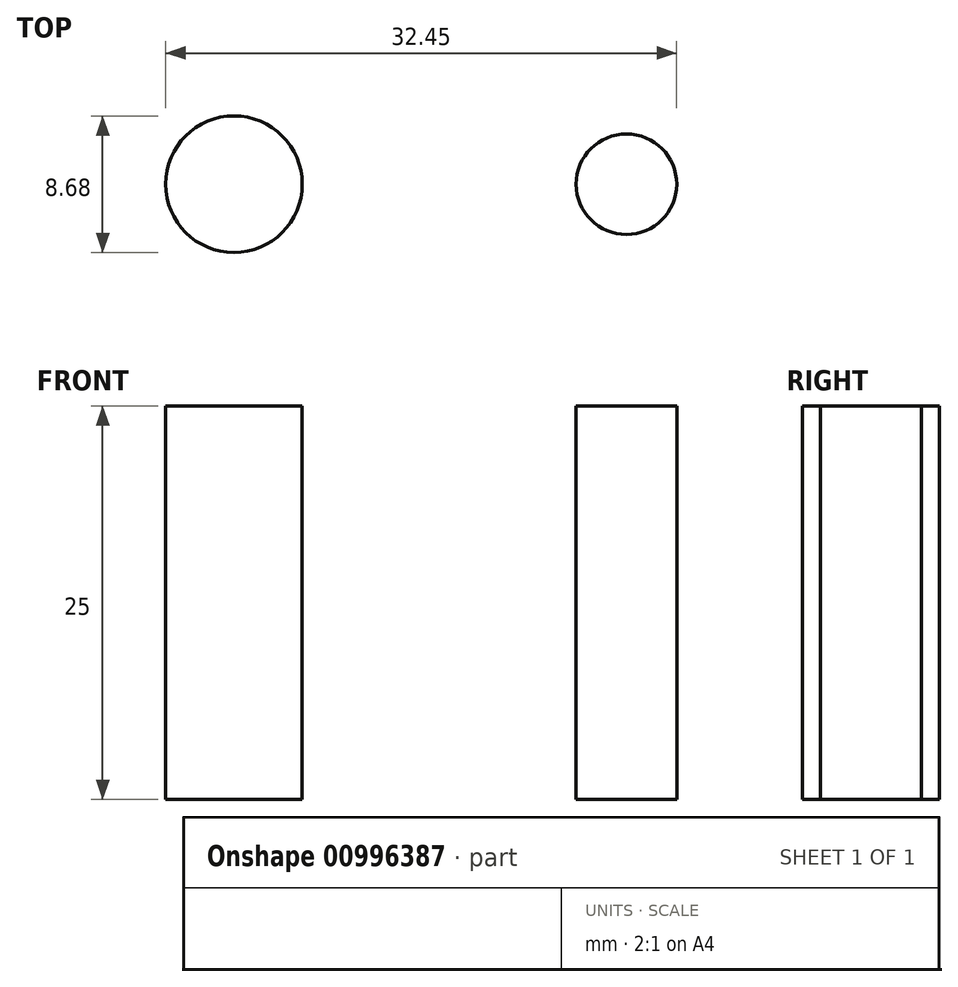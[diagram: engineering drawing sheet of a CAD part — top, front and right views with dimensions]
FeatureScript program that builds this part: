
annotation { "Feature Type Name" : "Feature", "Feature Type Description" : "" }
export const myFeature = defineFeature(function(context is Context, id is Id, definition is map)
    precondition{}
    {
        {
            var Q0;
            Q0=qCreatedBy(makeId("Top.planeOp"),FACE);
            var sketch = newSketch(context, id + "F0", { "sketchPlane" : qUnion([Q0])});
            skCircle(sketch, "E0", {"center": v(-14.2, 0) * mm, "radius": 4.34 * mm});
            skCircle(sketch, "E1", {"center": v(10.72, 0) * mm, "radius": 3.2 * mm});
            skSolve(sketch);
        }
        {
            var Q0;
            Q0 = qSketchRegion(id + "F0", true);
            extrude(context, id + "F1", {"entities" : qUnion([Q0]), "depth" : 25 * mm, "offsetDistance" : 25 * mm});
        }
    });
